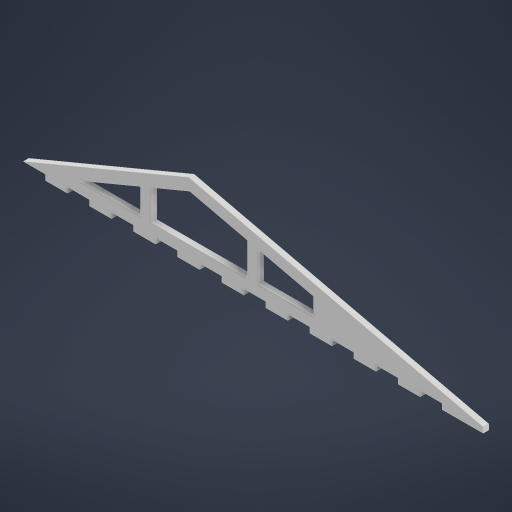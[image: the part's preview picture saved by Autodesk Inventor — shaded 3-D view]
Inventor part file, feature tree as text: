
AUTODESK INVENTOR PART (.ipt)
format: ipt  version: 2023.2 (Build 272271000, 271)  size: 334,848 bytes
history: native  units: mm
features: sketch x2
ambient origin geometry x8: Origin, YZ Plane, XZ Plane, XY Plane, X Axis, Y Axis, Z Axis, Center Point
bodies: Body1 (feature_tree)
feature tree (2):
  sketch  "Sketch1"  dims[d228=105.0deg d268=60.0mm]
  sketch  "Sketch2"  dims[d269=70.0mm d270=300.0mm d273=120.0mm d274=50.0mm d275=105.0deg d283=90.0mm d284=40.0mm d285=45.0mm d286=4.0mm d287=0.0mm d289=8.0mm d290=8.0mm d292=16.0mm d296=16.0mm d297=4.0mm d299=4.0mm d300=0.0mm d9=0.5mm d10=0.872665mm d11=0.5mm d12=0.872665mm d13=0.5mm d14=0.872665mm d27=0.5mm d28=0.872665mm d29=0.5mm d30=0.872665mm d88=0.5mm d89=0.872665mm d90=0.5mm d91=0.872665mm d116=0.5mm d117=0.872665mm d118=0.5mm d119=0.872665mm d154=0.5mm d155=0.872665mm d156=0.5mm d157=0.872665mm d181=0.5mm d182=0.872665mm d183=0.5mm d184=0.872665mm d221=0.5mm d222=0.872665mm d223=0.5mm d224=0.872665mm d301=0.5mm d302=0.872665mm d303=0.5mm d304=0.872665mm]
